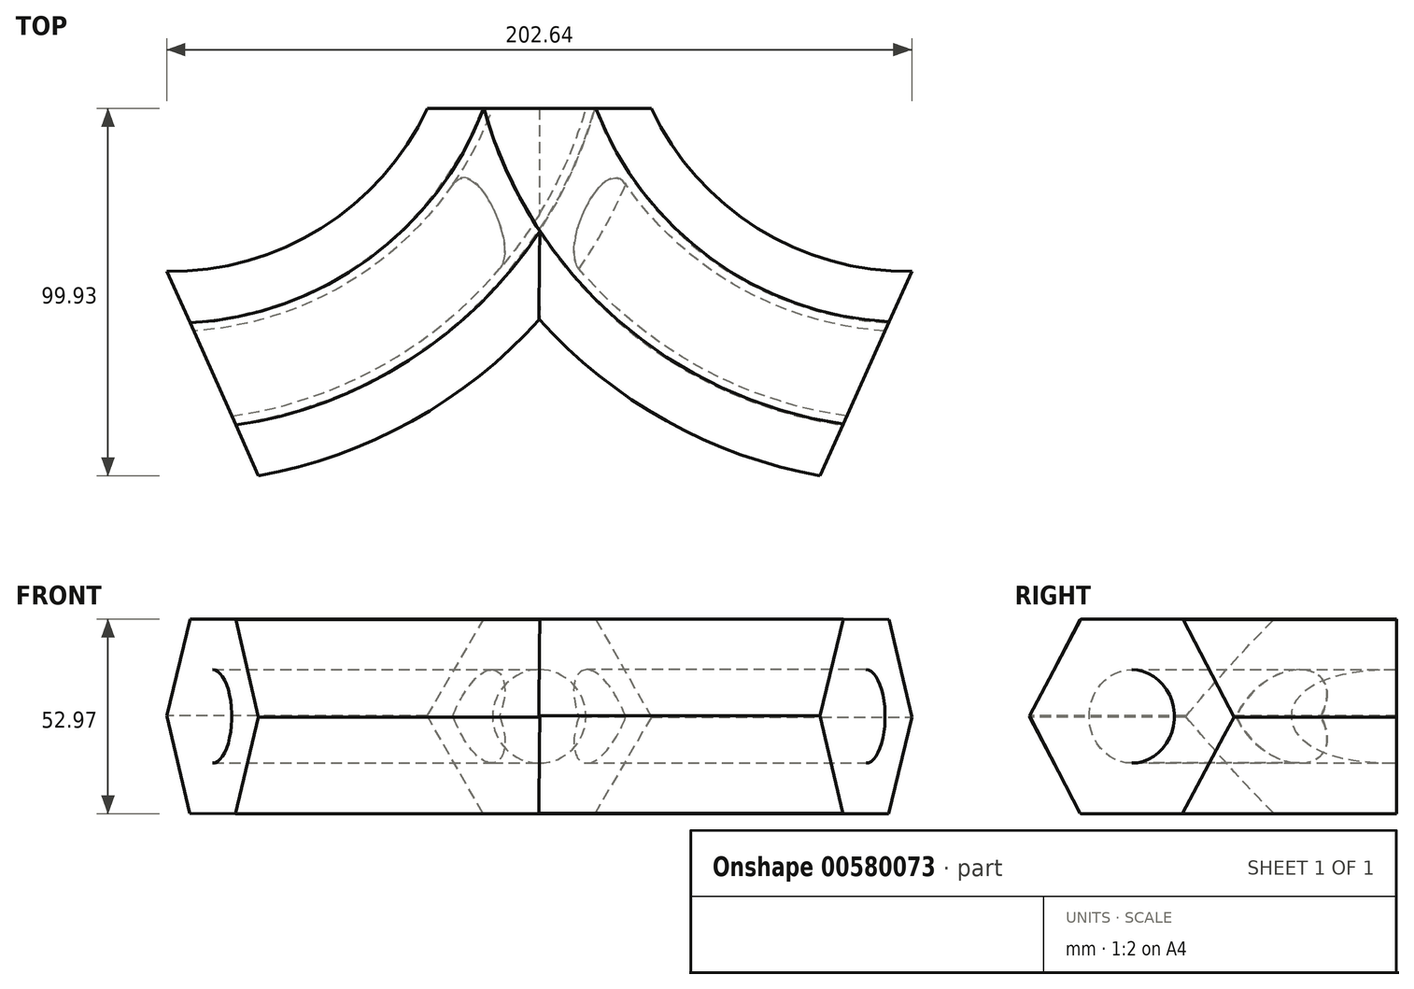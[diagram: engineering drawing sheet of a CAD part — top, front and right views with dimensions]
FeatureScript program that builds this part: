
annotation { "Feature Type Name" : "Feature", "Feature Type Description" : "" }
export const myFeature = defineFeature(function(context is Context, id is Id, definition is map)
    precondition{}
    {
        {
            var Q0;
            Q0=qCreatedBy(makeId("Front.planeOp"),FACE);
            var sketch = newSketch(context, id + "F0", { "sketchPlane" : qUnion([Q0])});
            skCircle(sketch, "E0.cCircle", {"center": v(0, 26.89) * mm, "radius": 26.4 * mm, "construction": true});
            skLineSegment(sketch, "E0.0", {"start": v(-15.4, 0.58) * mm, "end": v(-30.48, 27.07) * mm});
            skLineSegment(sketch, "E0.1", {"start": v(-30.48, 27.07) * mm, "end": v(-15.08, 53.37) * mm});
            skLineSegment(sketch, "E0.2", {"start": v(-15.08, 53.37) * mm, "end": v(15.4, 53.2) * mm});
            skLineSegment(sketch, "E0.3", {"start": v(15.4, 53.2) * mm, "end": v(30.48, 26.7) * mm});
            skLineSegment(sketch, "E0.4", {"start": v(30.48, 26.7) * mm, "end": v(15.08, 0.4) * mm});
            skLineSegment(sketch, "E0.5", {"start": v(15.08, 0.4) * mm, "end": v(-15.4, 0.58) * mm});
            skPoint(sketch, "E0.0.midPoint", {"position": v(-22.94, 13.82) * mm});
            skSolve(sketch);
        }
        {
            var Q0;
            Q0=qCreatedBy(makeId("Top.planeOp"),FACE);
            var sketch = newSketch(context, id + "F1", { "sketchPlane" : qUnion([Q0])});
            skArc(sketch, "E1", {"start": v(-88.86, -72.11) * mm, "mid": v(-33.77, -49.2) * mm, "end": v(0, 0) * mm});
            skArc(sketch, "E2.MirrorCS", {"start": v(88.86, -72.11) * mm, "mid": v(33.77, -49.2) * mm, "end": v(0, 0) * mm});
            skSolve(sketch);
        }
        {
            var Q0;
            Q0=makeQuery(id+"F0.imprint","IMPRINT",FACE,{"disambiguationData":[TD([[makeQuery(id+"F0.imprint","IMPRINT",EDGE,{"derivedFrom":sQuery(id+"F0.wireOp",EDGE,"E0.0")}),-1.0]])]});
            var sketch = newSketch(context, id + "F2", { "sketchPlane" : qUnion([Q0])});
            skCircle(sketch, "E3", {"center": v(0, 26.89) * mm, "radius": 12.7 * mm});
            skSolve(sketch);
        }
        {
            var Q0;
            Q0=makeQuery(id+"F2.imprint","IMPRINT",FACE,{"disambiguationData":[TD([[makeQuery(id+"F2.imprint","IMPRINT",EDGE,{"derivedFrom":sQuery(id+"F2.wireOp",EDGE,"E3")}),-1.0]])]});
            var Q1;
            Q1=sQuery(id+"F1.wireOp",EDGE,"E2.MirrorCS");
            sweep(context, id + "F3", {"profiles" : qUnion([Q0]), "path" : qUnion([Q1])});
        }
        {
            var Q0;
            Q0=makeQuery(id+"F2.imprint","IMPRINT",FACE,{"disambiguationData":[TD([[makeQuery(id+"F2.imprint","IMPRINT",EDGE,{"derivedFrom":sQuery(id+"F2.wireOp",EDGE,"E3")}),-1.0]])]});
            var Q1;
            Q1=sQuery(id+"F1.wireOp",EDGE,"E2.MirrorCS");
            sweep(context, id + "F4", {"profiles" : qUnion([Q0]), "path" : qUnion([Q1])});
        }
        {
            var Q0;
            Q0=makeQuery(id+"F4.opSweep","SWEPT_BODY",BODY,{"disambiguationData":[OSD([sQuery(id+"F0.wireOp",EDGE,"E0.0"),sQuery(id+"F0.wireOp",EDGE,"E0.1"),sQuery(id+"F0.wireOp",EDGE,"E0.2"),sQuery(id+"F0.wireOp",EDGE,"E0.3"),sQuery(id+"F0.wireOp",EDGE,"E0.4"),sQuery(id+"F0.wireOp",EDGE,"E0.5"),sQuery(id+"F1.wireOp",EDGE,"E2.MirrorCS"),sQuery(id+"F2.wireOp",EDGE,"E3")])]});
            deleteBodies(context, id + "F5", {"entities" : qUnion([Q0])});
        }
        {
            var Q0;
            Q0=makeQuery(id+"F2.imprint","IMPRINT",FACE,{"disambiguationData":[TD([[makeQuery(id+"F2.imprint","IMPRINT",EDGE,{"derivedFrom":sQuery(id+"F2.wireOp",EDGE,"E3")}),-1.0]])]});
            var Q1;
            Q1=sQuery(id+"F1.wireOp",EDGE,"E1");
            sweep(context, id + "F6", {"operationType" : NewBodyOperationType.ADD, "profiles" : qUnion([Q0]), "path" : qUnion([Q1])});
        }
        {
            var Q0;
            Q0=makeQuery(id+"F2.imprint","IMPRINT",FACE,{"disambiguationData":[TD([[makeQuery(id+"F2.imprint","IMPRINT",EDGE,{"derivedFrom":sQuery(id+"F2.wireOp",EDGE,"E3")}),1.0]])]});
            var Q1;
            Q1=sQuery(id+"F1.wireOp",EDGE,"E1");
            sweep(context, id + "F7", {"operationType" : NewBodyOperationType.REMOVE, "profiles" : qUnion([Q0]), "path" : qUnion([Q1])});
        }
    });
